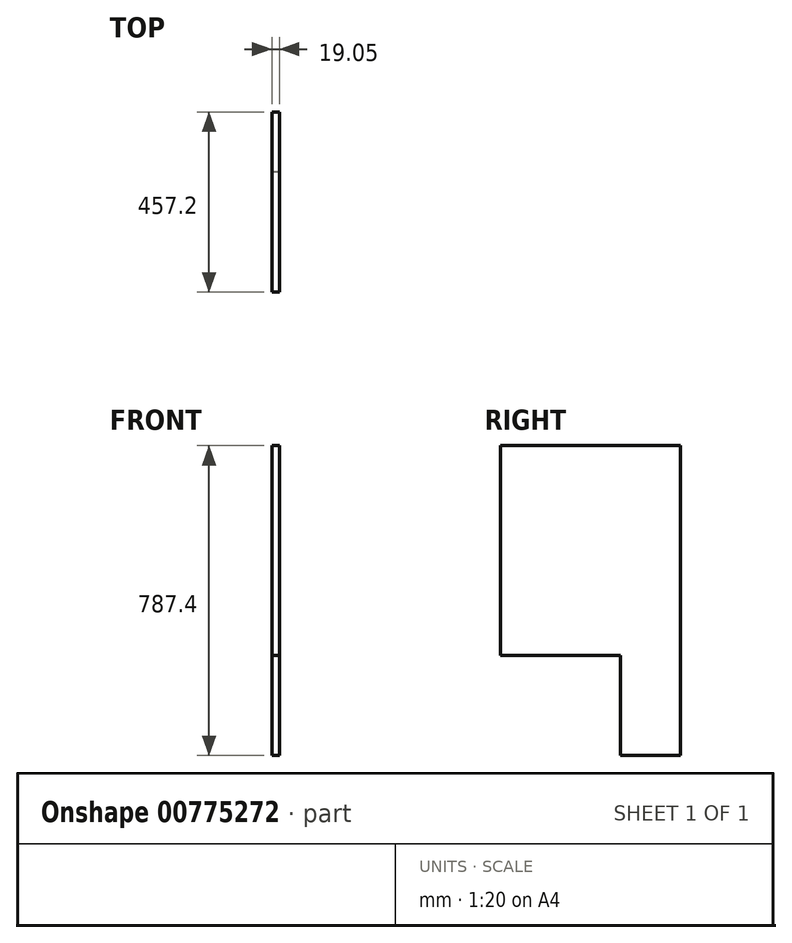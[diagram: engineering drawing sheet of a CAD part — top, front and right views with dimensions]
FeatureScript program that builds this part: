
annotation { "Feature Type Name" : "Feature", "Feature Type Description" : "" }
export const myFeature = defineFeature(function(context is Context, id is Id, definition is map)
    precondition{}
    {
        {
            var Q0;
            Q0=qCreatedBy(makeId("Right.planeOp"),FACE);
            var sketch = newSketch(context, id + "F0", { "sketchPlane" : qUnion([Q0])});
            skLineSegment(sketch, "E0.right", {"start": v(-304.8, 0) * mm, "end": v(-304.8, 533.4) * mm});
            skLineSegment(sketch, "E1", {"start": v(152.4, 533.4) * mm, "end": v(152.4, -254) * mm});
            skLineSegment(sketch, "E2", {"start": v(152.4, -254) * mm, "end": v(0, -254) * mm});
            skLineSegment(sketch, "E3", {"start": v(0, -254) * mm, "end": v(0, 0) * mm});
            skLineSegment(sketch, "E4", {"start": v(0, 0) * mm, "end": v(-304.8, 0) * mm});
            skLineSegment(sketch, "E5", {"start": v(-304.8, 533.4) * mm, "end": v(152.4, 533.4) * mm});
            skSolve(sketch);
        }
        {
            var Q0;
            Q0 = qSketchRegion(id + "F0", true);
            extrude(context, id + "F1", {"entities" : qUnion([Q0]), "depth" : 19.05 * mm, "offsetDistance" : 25.4 * mm});
        }
    });
